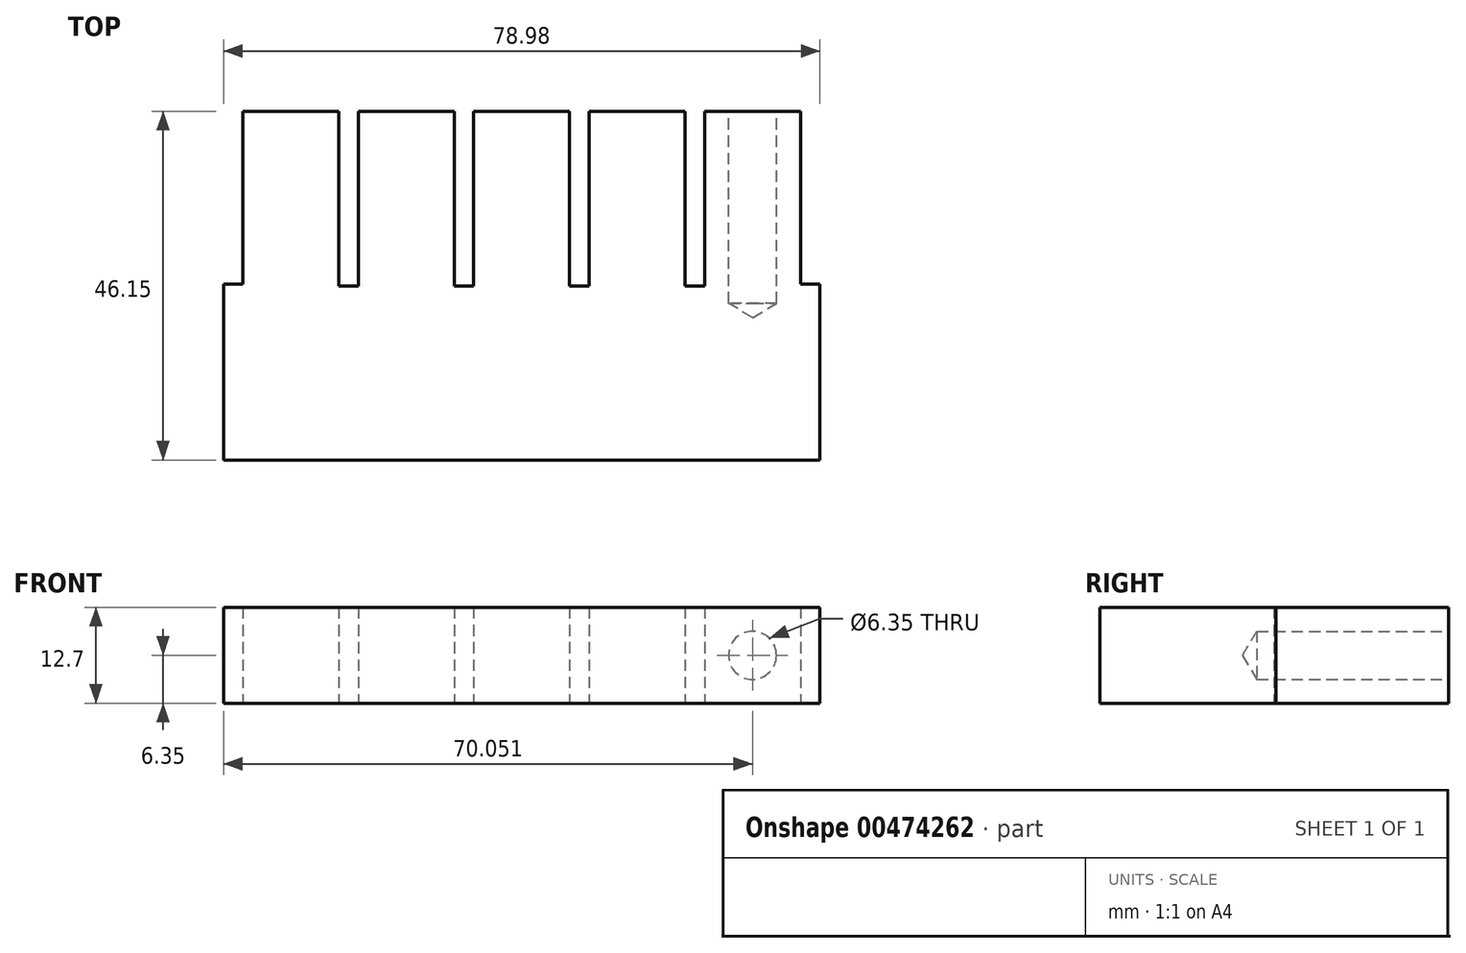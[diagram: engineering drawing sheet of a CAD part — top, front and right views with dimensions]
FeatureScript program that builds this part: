
annotation { "Feature Type Name" : "Feature", "Feature Type Description" : "" }
export const myFeature = defineFeature(function(context is Context, id is Id, definition is map)
    precondition{}
    {
        {
            var Q0;
            Q0=qCreatedBy(makeId("Top.planeOp"),FACE);
            var sketch = newSketch(context, id + "F0", { "sketchPlane" : qUnion([Q0])});
            skLineSegment(sketch, "E0", {"start": v(39.5, 0.23) * mm, "end": v(39.5, -23.04) * mm});
            skLineSegment(sketch, "E1", {"start": v(39.5, -23.04) * mm, "end": v(0, -23.04) * mm});
            skLineSegment(sketch, "E2", {"start": v(36.91, 0.23) * mm, "end": v(36.91, 23.1) * mm});
            skLineSegment(sketch, "E3", {"start": v(36.91, 23.1) * mm, "end": v(24.21, 23.1) * mm});
            skLineSegment(sketch, "E4", {"start": v(24.21, 23.1) * mm, "end": v(24.21, 0) * mm});
            skLineSegment(sketch, "E5", {"start": v(21.63, 0) * mm, "end": v(21.63, 23.1) * mm});
            skLineSegment(sketch, "E6", {"start": v(21.63, 23.1) * mm, "end": v(8.93, 23.1) * mm});
            skLineSegment(sketch, "E7", {"start": v(8.93, 23.1) * mm, "end": v(8.93, 0) * mm});
            skLineSegment(sketch, "E8", {"start": v(6.35, 0) * mm, "end": v(6.35, 23.1) * mm});
            skLineSegment(sketch, "E9", {"start": v(6.35, 23.1) * mm, "end": v(0, 23.1) * mm});
            skLineSegment(sketch, "E10", {"start": v(6.35, 0) * mm, "end": v(8.93, 0) * mm});
            skLineSegment(sketch, "E11", {"start": v(21.63, 0) * mm, "end": v(24.21, 0) * mm});
            skLineSegment(sketch, "E12", {"start": v(36.91, 0.23) * mm, "end": v(39.5, 0.23) * mm});
            skLineSegment(sketch, "E13.MirrorCS", {"start": v(-6.35, 23.1) * mm, "end": v(0, 23.1) * mm});
            skLineSegment(sketch, "E14.MirrorCS", {"start": v(-39.5, 0.23) * mm, "end": v(-39.5, -23.04) * mm});
            skLineSegment(sketch, "E15.MirrorCS", {"start": v(-6.35, 0) * mm, "end": v(-8.93, 0) * mm});
            skLineSegment(sketch, "E16.MirrorCS", {"start": v(-6.35, 0) * mm, "end": v(-6.35, 23.1) * mm});
            skLineSegment(sketch, "E17.MirrorCS", {"start": v(-39.5, -23.04) * mm, "end": v(0, -23.04) * mm});
            skLineSegment(sketch, "E18.MirrorCS", {"start": v(-8.93, 23.1) * mm, "end": v(-8.93, 0) * mm});
            skLineSegment(sketch, "E19.MirrorCS", {"start": v(-36.91, 0.23) * mm, "end": v(-39.5, 0.23) * mm});
            skLineSegment(sketch, "E20.MirrorCS", {"start": v(-21.63, 23.1) * mm, "end": v(-8.93, 23.1) * mm});
            skLineSegment(sketch, "E21.MirrorCS", {"start": v(-36.91, 0.23) * mm, "end": v(-36.91, 23.1) * mm});
            skLineSegment(sketch, "E22.MirrorCS", {"start": v(-24.21, 23.1) * mm, "end": v(-24.21, 0) * mm});
            skLineSegment(sketch, "E23.MirrorCS", {"start": v(-21.63, 0) * mm, "end": v(-24.21, 0) * mm});
            skLineSegment(sketch, "E24.MirrorCS", {"start": v(-21.63, 0) * mm, "end": v(-21.63, 23.1) * mm});
            skLineSegment(sketch, "E25.MirrorCS", {"start": v(-36.91, 23.1) * mm, "end": v(-24.21, 23.1) * mm});
            skSolve(sketch);
        }
        {
            var Q0;
            Q0=makeQuery(id+"F0.imprint","IMPRINT",FACE,{"disambiguationData":[TD([[makeQuery(id+"F0.imprint","IMPRINT",EDGE,{"derivedFrom":sQuery(id+"F0.wireOp",EDGE,"E0")}),-1.0]])]});
            extrude(context, id + "F1", {"entities" : qUnion([Q0]), "depth" : 12.7 * mm});
        }
        {
            var Q0;
            Q0=makeQuery(id+"F1.opExtrude","SWEPT_FACE",FACE,{"disambiguationData":[OSD([sQuery(id+"F0.wireOp",EDGE,"E3")])]});
            var sketch = newSketch(context, id + "F2", { "sketchPlane" : qUnion([Q0])});
            skCircle(sketch, "E26", {"center": v(-30.56, 6.35) * mm, "radius": 3.18 * mm});
            skSolve(sketch);
        }
        {
            var Q0;
            Q0=sQuery(id+"F2.wireOp",VERTEX,"E26.center");
            var Q1;
            Q1=makeQuery(id+"F1.opExtrude","SWEPT_BODY",BODY,{"disambiguationData":[OSD([sQuery(id+"F0.wireOp",EDGE,"E0"),sQuery(id+"F0.wireOp",EDGE,"E1"),sQuery(id+"F0.wireOp",EDGE,"E2"),sQuery(id+"F0.wireOp",EDGE,"E3"),sQuery(id+"F0.wireOp",EDGE,"E4"),sQuery(id+"F0.wireOp",EDGE,"E5"),sQuery(id+"F0.wireOp",EDGE,"E6"),sQuery(id+"F0.wireOp",EDGE,"E7"),sQuery(id+"F0.wireOp",EDGE,"E8"),sQuery(id+"F0.wireOp",EDGE,"E9"),sQuery(id+"F0.wireOp",EDGE,"E10"),sQuery(id+"F0.wireOp",EDGE,"E11"),sQuery(id+"F0.wireOp",EDGE,"E12"),sQuery(id+"F0.wireOp",EDGE,"E13.MirrorCS"),sQuery(id+"F0.wireOp",EDGE,"E14.MirrorCS"),sQuery(id+"F0.wireOp",EDGE,"E15.MirrorCS"),sQuery(id+"F0.wireOp",EDGE,"E16.MirrorCS"),sQuery(id+"F0.wireOp",EDGE,"E17.MirrorCS"),sQuery(id+"F0.wireOp",EDGE,"E18.MirrorCS"),sQuery(id+"F0.wireOp",EDGE,"E19.MirrorCS"),sQuery(id+"F0.wireOp",EDGE,"E20.MirrorCS"),sQuery(id+"F0.wireOp",EDGE,"E21.MirrorCS"),sQuery(id+"F0.wireOp",EDGE,"E22.MirrorCS"),sQuery(id+"F0.wireOp",EDGE,"E23.MirrorCS"),sQuery(id+"F0.wireOp",EDGE,"E24.MirrorCS"),sQuery(id+"F0.wireOp",EDGE,"E25.MirrorCS")])]});
            hole(context, id + "F3", {"style" : HoleStyle.SIMPLE, "endStyle" : HoleEndStyle.BLIND, "holeDiameter" : 6.35 * mm, "holeDepth" : 25.4 * mm, "isTappedThrough" : true, "tappedDepth" : 12.7 * mm, "tapClearance" : 3, "locations" : qUnion([Q0]), "scope" : qUnion([Q1])});
        }
    });
